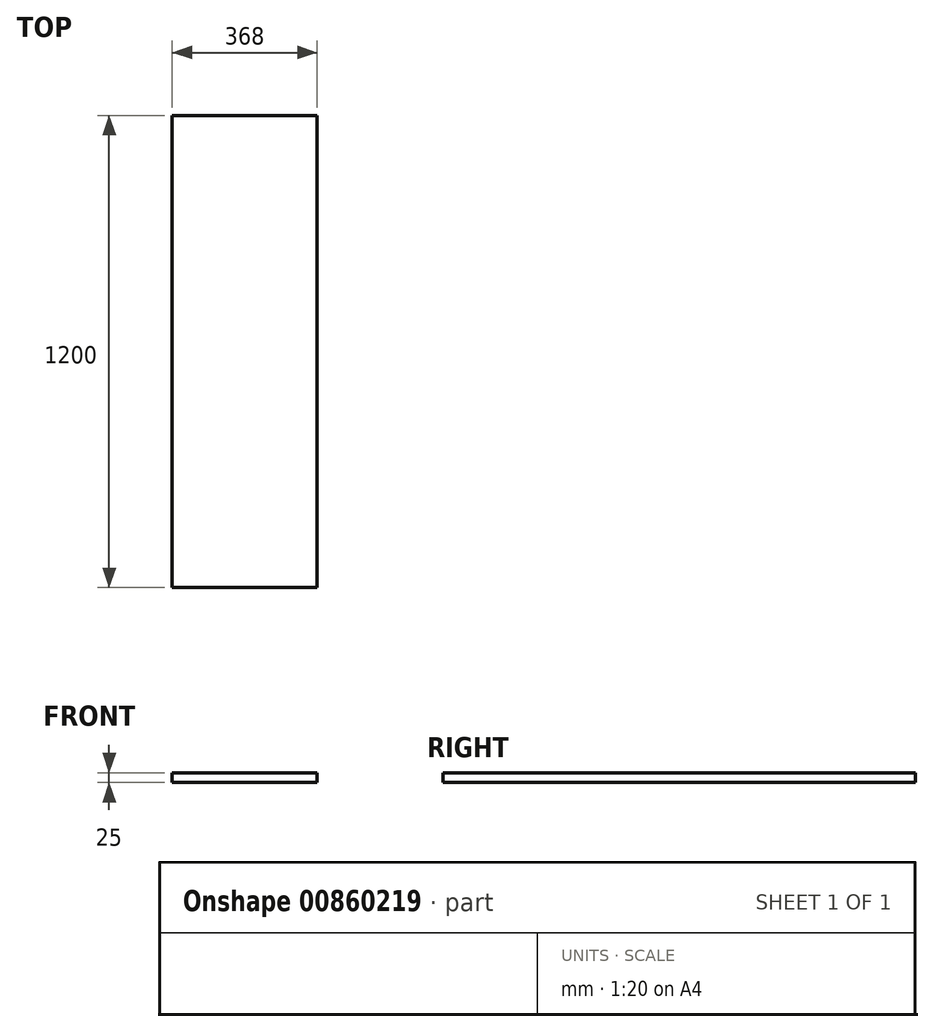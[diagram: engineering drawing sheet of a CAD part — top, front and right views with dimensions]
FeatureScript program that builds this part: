
annotation { "Feature Type Name" : "Feature", "Feature Type Description" : "" }
export const myFeature = defineFeature(function(context is Context, id is Id, definition is map)
    precondition{}
    {
        {
            var Q0;
            Q0=qCreatedBy(makeId("Top.planeOp"),FACE);
            var sketch = newSketch(context, id + "F0", { "sketchPlane" : qUnion([Q0])});
            skLineSegment(sketch, "E0.bottom", {"start": v(0, 0) * mm, "end": v(368, 0) * mm});
            skLineSegment(sketch, "E0.top", {"start": v(0, 1200) * mm, "end": v(368, 1200) * mm});
            skLineSegment(sketch, "E0.left", {"start": v(0, 0) * mm, "end": v(0, 1200) * mm});
            skLineSegment(sketch, "E0.right", {"start": v(368, 0) * mm, "end": v(368, 1200) * mm});
            skSolve(sketch);
        }
        {
            var Q0;
            Q0 = qSketchRegion(id + "F0", true);
            extrude(context, id + "F1", {"entities" : qUnion([Q0]), "depth" : 25 * mm, "offsetDistance" : 25 * mm});
        }
    });
